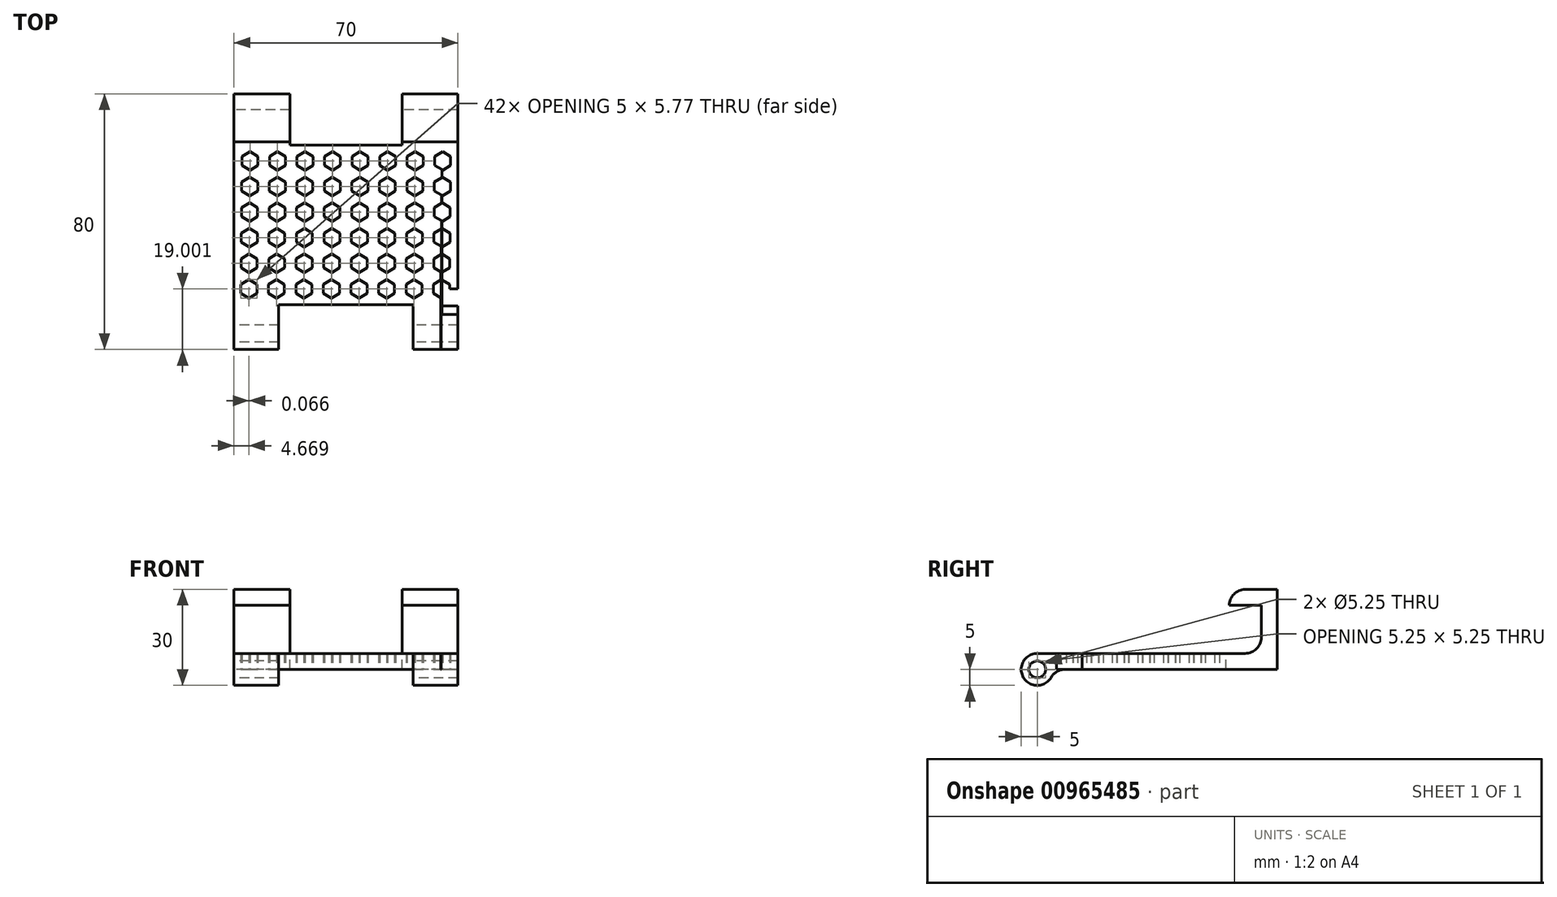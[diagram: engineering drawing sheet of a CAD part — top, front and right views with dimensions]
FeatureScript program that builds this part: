
annotation { "Feature Type Name" : "Feature", "Feature Type Description" : "" }
export const myFeature = defineFeature(function(context is Context, id is Id, definition is map)
    precondition{}
    {
        {
            var Q0;
            Q0=qCreatedBy(makeId("Right.planeOp"),FACE);
            var sketch = newSketch(context, id + "F0", { "sketchPlane" : qUnion([Q0])});
            skLineSegment(sketch, "E0", {"start": v(-20.34, 0) * mm, "end": v(0, 0) * mm, "construction": true});
            skLineSegment(sketch, "E1.0", {"start": v(-75, 14.81) * mm, "end": v(-75, 5) * mm, "construction": true});
            skLineSegment(sketch, "E2.0", {"start": v(-15, 25) * mm, "end": v(0, 25) * mm, "construction": true});
            skLineSegment(sketch, "E3.0", {"start": v(-20.34, 5) * mm, "end": v(-5, 5) * mm});
            skLineSegment(sketch, "E4", {"start": v(-20.34, 5) * mm, "end": v(-75, 5) * mm});
            skLineSegment(sketch, "E5", {"start": v(-66.34, 0) * mm, "end": v(0, 0) * mm});
            skLineSegment(sketch, "E6", {"start": v(0, 25) * mm, "end": v(-15, 25) * mm});
            skLineSegment(sketch, "E7", {"start": v(-15, 25) * mm, "end": v(-15, 20) * mm});
            skLineSegment(sketch, "E8", {"start": v(-15, 20) * mm, "end": v(-5, 20) * mm});
            skLineSegment(sketch, "E9", {"start": v(-5, 20) * mm, "end": v(-5, 5) * mm});
            skPoint(sketch, "E10.orphan", {"position": v(0, 14.81) * mm});
            skPoint(sketch, "E11.orphan", {"position": v(20.06, 25) * mm});
            skPoint(sketch, "E12.orphan", {"position": v(-20.06, 25) * mm});
            skLineSegment(sketch, "E13", {"start": v(0, 25) * mm, "end": v(0, 5) * mm});
            skLineSegment(sketch, "E14", {"start": v(0, 5) * mm, "end": v(0, 0) * mm});
            skArc(sketch, "E15", {"start": v(-75, 5) * mm, "mid": v(-79.33, -2.5) * mm, "end": v(-70.67, -2.5) * mm});
            skLineSegment(sketch, "E16.trimOffspring", {"start": v(-75, 0) * mm, "end": v(-75, -12.94) * mm, "construction": true});
            skCircle(sketch, "E17", {"center": v(-75, 0) * mm, "radius": 2.62 * mm});
            skPoint(sketch, "E18.visualSharp", {"position": v(-70, 0) * mm});
            skArc(sketch, "E18.filletArc", {"start": v(-66.34, 0) * mm, "mid": v(-68.84, -0.67) * mm, "end": v(-70.67, -2.5) * mm});
            skSolve(sketch);
        }
        {
            var Q0;
            Q0=makeQuery(id+"F0.imprint","IMPRINT",FACE,{"disambiguationData":[TD([[makeQuery(id+"F0.imprint","IMPRINT",EDGE,{"derivedFrom":sQuery(id+"F0.wireOp",EDGE,"E3.0")}),-1.0]])]});
            extrude(context, id + "F1", {"entities" : qUnion([Q0]), "depth" : 70 * mm, "offsetDistance" : 25 * mm});
        }
        {
            var Q0;
            Q0=qCreatedBy(makeId("Front.planeOp"),FACE);
            var sketch = newSketch(context, id + "F2", { "sketchPlane" : qUnion([Q0])});
            skLineSegment(sketch, "E19", {"start": v(0, 0) * mm, "end": v(0, 33.65) * mm, "construction": true});
            skLineSegment(sketch, "E20", {"start": v(0, 0) * mm, "end": v(85.21, 0) * mm, "construction": true});
            skLineSegment(sketch, "E21.0", {"start": v(17.5, 0) * mm, "end": v(17.5, 33.65) * mm, "construction": true});
            skLineSegment(sketch, "E22.0", {"start": v(0, 5) * mm, "end": v(85.21, 5) * mm, "construction": true});
            skLineSegment(sketch, "E23.bottom", {"start": v(17.5, 0) * mm, "end": v(52.5, 0) * mm});
            skLineSegment(sketch, "E23.top", {"start": v(17.5, 25) * mm, "end": v(52.5, 25) * mm});
            skLineSegment(sketch, "E23.left", {"start": v(17.5, 0) * mm, "end": v(17.5, 25) * mm});
            skLineSegment(sketch, "E23.right", {"start": v(52.5, 0) * mm, "end": v(52.5, 25) * mm});
            skSolve(sketch);
        }
        {
            var Q0;
            Q0 = qSketchRegion(id + "F2", true);
            extrude(context, id + "F3", {"entities" : qUnion([Q0]), "operationType" : NewBodyOperationType.REMOVE, "depth" : 16 * mm, "offsetDistance" : 25 * mm});
        }
        {
            var Q0;
            Q0=qCreatedBy(makeId("Front.planeOp"),FACE);
            cPlane(context, id + "F4", {"entities" : qUnion([Q0]), "cplaneType" : CPlaneType.OFFSET, "offset" : 75 * mm, "width" : 150 * mm, "height" : 150 * mm});
        }
        {
            var Q0;
            Q0=qCreatedBy(id+"F4.planeOp",FACE);
            var sketch = newSketch(context, id + "F5", { "sketchPlane" : qUnion([Q0])});
            skLineSegment(sketch, "E24", {"start": v(0, 31.01) * mm, "end": v(0, -27.06) * mm, "construction": true});
            skLineSegment(sketch, "E25.0", {"start": v(14, 31.01) * mm, "end": v(14, -27.06) * mm, "construction": true});
            skLineSegment(sketch, "E26.0", {"start": v(28, 31.01) * mm, "end": v(28, -27.06) * mm, "construction": true});
            skLineSegment(sketch, "E27.0", {"start": v(42, 31.01) * mm, "end": v(42, -27.06) * mm, "construction": true});
            skLineSegment(sketch, "E28.0", {"start": v(56, 31.01) * mm, "end": v(56, -27.06) * mm, "construction": true});
            skLineSegment(sketch, "E29.0", {"start": v(70, 31.01) * mm, "end": v(70, -27.06) * mm, "construction": true});
            skLineSegment(sketch, "E30.bottom", {"start": v(14, 5) * mm, "end": v(56, 5) * mm});
            skLineSegment(sketch, "E30.top", {"start": v(14, -5) * mm, "end": v(56, -5) * mm});
            skLineSegment(sketch, "E30.left", {"start": v(14, 5) * mm, "end": v(14, -5) * mm});
            skLineSegment(sketch, "E30.right", {"start": v(56, 5) * mm, "end": v(56, -5) * mm});
            skSolve(sketch);
        }
        {
            var Q0;
            Q0 = qSketchRegion(id + "F5", true);
            extrude(context, id + "F6", {"entities" : qUnion([Q0]), "operationType" : NewBodyOperationType.REMOVE, "oppositeDirection" : true, "depth" : 9 * mm, "offsetDistance" : 25 * mm, "hasSecondDirection" : true, "secondDirectionBound" : SecondDirectionBoundingType.THROUGH_ALL, "secondDirectionOppositeDirection" : false, "secondDirectionDepth" : 8 * mm});
        }
        {
            var Q0;
            {var subQ1=sQuery(id+"F0.wireOp",EDGE,"E3.0");var subQ2=sQuery(id+"F0.wireOp",EDGE,"E9");Q0=makeQuery(id+"F3.boolean.opBoolean","SPLIT",EDGE,{"disambiguationData":[TD([makeQuery(id+"F3.opExtrude","SWEPT_FACE",FACE,{"disambiguationData":[OSD([sQuery(id+"F2.wireOp",EDGE,"E23.left")])]})])],"derivedFrom":makeQuery(id+"F1.opExtrude","SWEPT_EDGE",EDGE,{"disambiguationData":[OSD([subQ1,subQ2])]})});}
            var Q1;
            {var subQ1=sQuery(id+"F0.wireOp",EDGE,"E3.0");var subQ2=sQuery(id+"F0.wireOp",EDGE,"E9");Q1=makeQuery(id+"F3.boolean.opBoolean","SPLIT",EDGE,{"disambiguationData":[TD([makeQuery(id+"F3.opExtrude","SWEPT_FACE",FACE,{"disambiguationData":[OSD([sQuery(id+"F2.wireOp",EDGE,"E23.right")])]})])],"derivedFrom":makeQuery(id+"F1.opExtrude","SWEPT_EDGE",EDGE,{"disambiguationData":[OSD([subQ1,subQ2])]})});}
            fillet(context, id + "F7", {"entities" : qUnion([Q0, Q1]), "radius" : 5 * mm, "tangentPropagation" : true, "allowEdgeOverflow" : false});
        }
        {
            var Q0;
            {var subQ0=sQuery(id+"F0.wireOp",EDGE,"E7");var subQ1=sQuery(id+"F0.wireOp",EDGE,"E6");Q0=makeQuery(id+"F3.boolean.opBoolean","SPLIT",EDGE,{"disambiguationData":[TD([makeQuery(id+"F3.opExtrude","SWEPT_FACE",FACE,{"disambiguationData":[OSD([sQuery(id+"F2.wireOp",EDGE,"E23.left")])]})])],"derivedFrom":makeQuery(id+"F1.opExtrude","SWEPT_EDGE",EDGE,{"disambiguationData":[OSD([subQ1,subQ0])]})});}
            var Q1;
            {var subQ0=sQuery(id+"F0.wireOp",EDGE,"E7");var subQ1=sQuery(id+"F0.wireOp",EDGE,"E6");Q1=makeQuery(id+"F3.boolean.opBoolean","SPLIT",EDGE,{"disambiguationData":[TD([makeQuery(id+"F3.opExtrude","SWEPT_FACE",FACE,{"disambiguationData":[OSD([sQuery(id+"F2.wireOp",EDGE,"E23.right")])]})])],"derivedFrom":makeQuery(id+"F1.opExtrude","SWEPT_EDGE",EDGE,{"disambiguationData":[OSD([subQ1,subQ0])]})});}
            fillet(context, id + "F8", {"entities" : qUnion([Q0, Q1]), "radius" : 5 * mm, "tangentPropagation" : true, "allowEdgeOverflow" : false});
        }
        {
            var Q0;
            Q0=qCreatedBy(makeId("Top.planeOp"),FACE);
            var sketch = newSketch(context, id + "F9", { "sketchPlane" : qUnion([Q0])});
            skLineSegment(sketch, "E31", {"start": v(17.5, -16) * mm, "end": v(-16.9, -16) * mm, "construction": true});
            skLineSegment(sketch, "E32", {"start": v(0, -9.91) * mm, "end": v(0, -88.84) * mm, "construction": true});
            skLineSegment(sketch, "E33.0", {"start": v(5, -4.91) * mm, "end": v(5, -83.84) * mm, "construction": true});
            skLineSegment(sketch, "E34.0", {"start": v(17.5, -21) * mm, "end": v(-16.9, -21) * mm, "construction": true});
            skLineSegment(sketch, "E35.0", {"start": v(2.5, -19.56) * mm, "end": v(5, -18.11) * mm});
            skLineSegment(sketch, "E35.1", {"start": v(5, -18.11) * mm, "end": v(7.5, -19.56) * mm});
            skLineSegment(sketch, "E35.2", {"start": v(7.5, -19.56) * mm, "end": v(7.5, -22.44) * mm});
            skLineSegment(sketch, "E35.3", {"start": v(7.5, -22.44) * mm, "end": v(5, -23.89) * mm});
            skLineSegment(sketch, "E35.4", {"start": v(5, -23.89) * mm, "end": v(2.5, -22.44) * mm});
            skLineSegment(sketch, "E35.5", {"start": v(2.5, -22.44) * mm, "end": v(2.5, -19.56) * mm});
            skPoint(sketch, "E35.0.midPoint", {"position": v(3.75, -18.83) * mm});
            skLineSegment(sketch, "E36", {"start": v(70, -84.15) * mm, "end": v(70, -10.08) * mm, "construction": true});
            skLineSegment(sketch, "E37", {"start": v(-10.15, -66) * mm, "end": v(71.85, -66) * mm, "construction": true});
            skLineSegment(sketch, "E38.0", {"start": v(-10.15, -61) * mm, "end": v(71.85, -61) * mm});
            skLineSegment(sketch, "E39.0", {"start": v(65, -84.15) * mm, "end": v(65, -10.08) * mm});
            skLineSegment(sketch, "E40.0.1.0", {"start": v(-10.22, -69) * mm, "end": v(71.78, -69) * mm});
            skLineSegment(sketch, "E40.0.1.1", {"start": v(64.93, -92.15) * mm, "end": v(64.93, -18.08) * mm});
            skLineSegment(sketch, "E40.0.1.2", {"start": v(2.43, -30.44) * mm, "end": v(2.43, -27.56) * mm});
            skLineSegment(sketch, "E40.0.1.3", {"start": v(4.93, -31.89) * mm, "end": v(2.43, -30.44) * mm});
            skLineSegment(sketch, "E40.0.1.4", {"start": v(7.43, -30.44) * mm, "end": v(4.93, -31.89) * mm});
            skLineSegment(sketch, "E40.0.1.5", {"start": v(7.43, -27.56) * mm, "end": v(7.43, -30.44) * mm});
            skLineSegment(sketch, "E40.0.1.6", {"start": v(4.93, -26.11) * mm, "end": v(7.43, -27.56) * mm});
            skLineSegment(sketch, "E40.0.1.7", {"start": v(2.43, -27.56) * mm, "end": v(4.93, -26.11) * mm});
            skLineSegment(sketch, "E40.0.2.0", {"start": v(-10.28, -77) * mm, "end": v(71.72, -77) * mm});
            skLineSegment(sketch, "E40.0.2.1", {"start": v(64.87, -100.15) * mm, "end": v(64.87, -26.08) * mm});
            skLineSegment(sketch, "E40.0.2.2", {"start": v(2.37, -38.44) * mm, "end": v(2.37, -35.56) * mm});
            skLineSegment(sketch, "E40.0.2.3", {"start": v(4.87, -39.89) * mm, "end": v(2.37, -38.44) * mm});
            skLineSegment(sketch, "E40.0.2.4", {"start": v(7.37, -38.44) * mm, "end": v(4.87, -39.89) * mm});
            skLineSegment(sketch, "E40.0.2.5", {"start": v(7.37, -35.56) * mm, "end": v(7.37, -38.44) * mm});
            skLineSegment(sketch, "E40.0.2.6", {"start": v(4.87, -34.11) * mm, "end": v(7.37, -35.56) * mm});
            skLineSegment(sketch, "E40.0.2.7", {"start": v(2.37, -35.56) * mm, "end": v(4.87, -34.11) * mm});
            skLineSegment(sketch, "E40.0.3.0", {"start": v(-10.35, -85) * mm, "end": v(71.65, -85) * mm});
            skLineSegment(sketch, "E40.0.3.1", {"start": v(64.8, -108.15) * mm, "end": v(64.8, -34.08) * mm});
            skLineSegment(sketch, "E40.0.3.2", {"start": v(2.3, -46.44) * mm, "end": v(2.3, -43.56) * mm});
            skLineSegment(sketch, "E40.0.3.3", {"start": v(4.8, -47.89) * mm, "end": v(2.3, -46.44) * mm});
            skLineSegment(sketch, "E40.0.3.4", {"start": v(7.3, -46.44) * mm, "end": v(4.8, -47.89) * mm});
            skLineSegment(sketch, "E40.0.3.5", {"start": v(7.3, -43.56) * mm, "end": v(7.3, -46.44) * mm});
            skLineSegment(sketch, "E40.0.3.6", {"start": v(4.8, -42.11) * mm, "end": v(7.3, -43.56) * mm});
            skLineSegment(sketch, "E40.0.3.7", {"start": v(2.3, -43.56) * mm, "end": v(4.8, -42.11) * mm});
            skLineSegment(sketch, "E40.0.4.0", {"start": v(-10.42, -93) * mm, "end": v(71.58, -93) * mm});
            skLineSegment(sketch, "E40.0.4.1", {"start": v(64.74, -116.15) * mm, "end": v(64.74, -42.08) * mm});
            skLineSegment(sketch, "E40.0.4.2", {"start": v(2.24, -54.44) * mm, "end": v(2.24, -51.56) * mm});
            skLineSegment(sketch, "E40.0.4.3", {"start": v(4.74, -55.89) * mm, "end": v(2.24, -54.44) * mm});
            skLineSegment(sketch, "E40.0.4.4", {"start": v(7.24, -54.44) * mm, "end": v(4.74, -55.89) * mm});
            skLineSegment(sketch, "E40.0.4.5", {"start": v(7.24, -51.56) * mm, "end": v(7.24, -54.44) * mm});
            skLineSegment(sketch, "E40.0.4.6", {"start": v(4.74, -50.11) * mm, "end": v(7.24, -51.56) * mm});
            skLineSegment(sketch, "E40.0.4.7", {"start": v(2.24, -51.56) * mm, "end": v(4.74, -50.11) * mm});
            skLineSegment(sketch, "E40.0.5.0", {"start": v(-10.48, -101) * mm, "end": v(71.52, -101) * mm});
            skLineSegment(sketch, "E40.0.5.1", {"start": v(64.67, -124.15) * mm, "end": v(64.67, -50.08) * mm});
            skLineSegment(sketch, "E40.0.5.2", {"start": v(2.17, -62.44) * mm, "end": v(2.17, -59.56) * mm});
            skLineSegment(sketch, "E40.0.5.3", {"start": v(4.67, -63.89) * mm, "end": v(2.17, -62.44) * mm});
            skLineSegment(sketch, "E40.0.5.4", {"start": v(7.17, -62.44) * mm, "end": v(4.67, -63.89) * mm});
            skLineSegment(sketch, "E40.0.5.5", {"start": v(7.17, -59.56) * mm, "end": v(7.17, -62.44) * mm});
            skLineSegment(sketch, "E40.0.5.6", {"start": v(4.67, -58.11) * mm, "end": v(7.17, -59.56) * mm});
            skLineSegment(sketch, "E40.0.5.7", {"start": v(2.17, -59.56) * mm, "end": v(4.67, -58.11) * mm});
            skLineSegment(sketch, "E40.1.0.0", {"start": v(-1.55, -61) * mm, "end": v(80.45, -61) * mm});
            skLineSegment(sketch, "E40.1.0.1", {"start": v(73.6, -84.15) * mm, "end": v(73.6, -10.08) * mm});
            skLineSegment(sketch, "E40.1.0.2", {"start": v(11.1, -22.44) * mm, "end": v(11.1, -19.56) * mm});
            skLineSegment(sketch, "E40.1.0.3", {"start": v(13.6, -23.89) * mm, "end": v(11.1, -22.44) * mm});
            skLineSegment(sketch, "E40.1.0.4", {"start": v(16.1, -22.44) * mm, "end": v(13.6, -23.89) * mm});
            skLineSegment(sketch, "E40.1.0.5", {"start": v(16.1, -19.56) * mm, "end": v(16.1, -22.44) * mm});
            skLineSegment(sketch, "E40.1.0.6", {"start": v(13.6, -18.11) * mm, "end": v(16.1, -19.56) * mm});
            skLineSegment(sketch, "E40.1.0.7", {"start": v(11.1, -19.56) * mm, "end": v(13.6, -18.11) * mm});
            skLineSegment(sketch, "E40.1.1.0", {"start": v(-1.62, -69) * mm, "end": v(80.38, -69) * mm});
            skLineSegment(sketch, "E40.1.1.1", {"start": v(73.53, -92.15) * mm, "end": v(73.53, -18.08) * mm});
            skLineSegment(sketch, "E40.1.1.2", {"start": v(11.03, -30.44) * mm, "end": v(11.03, -27.56) * mm});
            skLineSegment(sketch, "E40.1.1.3", {"start": v(13.53, -31.89) * mm, "end": v(11.03, -30.44) * mm});
            skLineSegment(sketch, "E40.1.1.4", {"start": v(16.03, -30.44) * mm, "end": v(13.53, -31.89) * mm});
            skLineSegment(sketch, "E40.1.1.5", {"start": v(16.03, -27.56) * mm, "end": v(16.03, -30.44) * mm});
            skLineSegment(sketch, "E40.1.1.6", {"start": v(13.53, -26.11) * mm, "end": v(16.03, -27.56) * mm});
            skLineSegment(sketch, "E40.1.1.7", {"start": v(11.03, -27.56) * mm, "end": v(13.53, -26.11) * mm});
            skLineSegment(sketch, "E40.1.2.0", {"start": v(-1.68, -77) * mm, "end": v(80.32, -77) * mm});
            skLineSegment(sketch, "E40.1.2.1", {"start": v(73.47, -100.15) * mm, "end": v(73.47, -26.08) * mm});
            skLineSegment(sketch, "E40.1.2.2", {"start": v(10.97, -38.44) * mm, "end": v(10.97, -35.56) * mm});
            skLineSegment(sketch, "E40.1.2.3", {"start": v(13.47, -39.89) * mm, "end": v(10.97, -38.44) * mm});
            skLineSegment(sketch, "E40.1.2.4", {"start": v(15.97, -38.44) * mm, "end": v(13.47, -39.89) * mm});
            skLineSegment(sketch, "E40.1.2.5", {"start": v(15.97, -35.56) * mm, "end": v(15.97, -38.44) * mm});
            skLineSegment(sketch, "E40.1.2.6", {"start": v(13.47, -34.11) * mm, "end": v(15.97, -35.56) * mm});
            skLineSegment(sketch, "E40.1.2.7", {"start": v(10.97, -35.56) * mm, "end": v(13.47, -34.11) * mm});
            skLineSegment(sketch, "E40.1.3.0", {"start": v(-1.75, -85) * mm, "end": v(80.25, -85) * mm});
            skLineSegment(sketch, "E40.1.3.1", {"start": v(73.4, -108.15) * mm, "end": v(73.4, -34.08) * mm});
            skLineSegment(sketch, "E40.1.3.2", {"start": v(10.9, -46.44) * mm, "end": v(10.9, -43.56) * mm});
            skLineSegment(sketch, "E40.1.3.3", {"start": v(13.4, -47.89) * mm, "end": v(10.9, -46.44) * mm});
            skLineSegment(sketch, "E40.1.3.4", {"start": v(15.9, -46.44) * mm, "end": v(13.4, -47.89) * mm});
            skLineSegment(sketch, "E40.1.3.5", {"start": v(15.9, -43.56) * mm, "end": v(15.9, -46.44) * mm});
            skLineSegment(sketch, "E40.1.3.6", {"start": v(13.4, -42.11) * mm, "end": v(15.9, -43.56) * mm});
            skLineSegment(sketch, "E40.1.3.7", {"start": v(10.9, -43.56) * mm, "end": v(13.4, -42.11) * mm});
            skLineSegment(sketch, "E40.1.4.0", {"start": v(-1.82, -93) * mm, "end": v(80.18, -93) * mm});
            skLineSegment(sketch, "E40.1.4.1", {"start": v(73.34, -116.15) * mm, "end": v(73.34, -42.08) * mm});
            skLineSegment(sketch, "E40.1.4.2", {"start": v(10.84, -54.44) * mm, "end": v(10.84, -51.56) * mm});
            skLineSegment(sketch, "E40.1.4.3", {"start": v(13.34, -55.89) * mm, "end": v(10.84, -54.44) * mm});
            skLineSegment(sketch, "E40.1.4.4", {"start": v(15.84, -54.44) * mm, "end": v(13.34, -55.89) * mm});
            skLineSegment(sketch, "E40.1.4.5", {"start": v(15.84, -51.56) * mm, "end": v(15.84, -54.44) * mm});
            skLineSegment(sketch, "E40.1.4.6", {"start": v(13.34, -50.11) * mm, "end": v(15.84, -51.56) * mm});
            skLineSegment(sketch, "E40.1.4.7", {"start": v(10.84, -51.56) * mm, "end": v(13.34, -50.11) * mm});
            skLineSegment(sketch, "E40.1.5.0", {"start": v(-1.88, -101) * mm, "end": v(80.12, -101) * mm});
            skLineSegment(sketch, "E40.1.5.1", {"start": v(73.27, -124.15) * mm, "end": v(73.27, -50.08) * mm});
            skLineSegment(sketch, "E40.1.5.2", {"start": v(10.77, -62.44) * mm, "end": v(10.77, -59.56) * mm});
            skLineSegment(sketch, "E40.1.5.3", {"start": v(13.27, -63.89) * mm, "end": v(10.77, -62.44) * mm});
            skLineSegment(sketch, "E40.1.5.4", {"start": v(15.77, -62.44) * mm, "end": v(13.27, -63.89) * mm});
            skLineSegment(sketch, "E40.1.5.5", {"start": v(15.77, -59.56) * mm, "end": v(15.77, -62.44) * mm});
            skLineSegment(sketch, "E40.1.5.6", {"start": v(13.27, -58.11) * mm, "end": v(15.77, -59.56) * mm});
            skLineSegment(sketch, "E40.1.5.7", {"start": v(10.77, -59.56) * mm, "end": v(13.27, -58.11) * mm});
            skLineSegment(sketch, "E40.2.0.0", {"start": v(7.05, -61) * mm, "end": v(89.05, -61) * mm});
            skLineSegment(sketch, "E40.2.0.1", {"start": v(82.2, -84.15) * mm, "end": v(82.2, -10.08) * mm});
            skLineSegment(sketch, "E40.2.0.2", {"start": v(19.7, -22.44) * mm, "end": v(19.7, -19.56) * mm});
            skLineSegment(sketch, "E40.2.0.3", {"start": v(22.2, -23.89) * mm, "end": v(19.7, -22.44) * mm});
            skLineSegment(sketch, "E40.2.0.4", {"start": v(24.7, -22.44) * mm, "end": v(22.2, -23.89) * mm});
            skLineSegment(sketch, "E40.2.0.5", {"start": v(24.7, -19.56) * mm, "end": v(24.7, -22.44) * mm});
            skLineSegment(sketch, "E40.2.0.6", {"start": v(22.2, -18.11) * mm, "end": v(24.7, -19.56) * mm});
            skLineSegment(sketch, "E40.2.0.7", {"start": v(19.7, -19.56) * mm, "end": v(22.2, -18.11) * mm});
            skLineSegment(sketch, "E40.2.1.0", {"start": v(6.98, -69) * mm, "end": v(88.98, -69) * mm});
            skLineSegment(sketch, "E40.2.1.1", {"start": v(82.13, -92.15) * mm, "end": v(82.13, -18.08) * mm});
            skLineSegment(sketch, "E40.2.1.2", {"start": v(19.63, -30.44) * mm, "end": v(19.63, -27.56) * mm});
            skLineSegment(sketch, "E40.2.1.3", {"start": v(22.13, -31.89) * mm, "end": v(19.63, -30.44) * mm});
            skLineSegment(sketch, "E40.2.1.4", {"start": v(24.63, -30.44) * mm, "end": v(22.13, -31.89) * mm});
            skLineSegment(sketch, "E40.2.1.5", {"start": v(24.63, -27.56) * mm, "end": v(24.63, -30.44) * mm});
            skLineSegment(sketch, "E40.2.1.6", {"start": v(22.13, -26.11) * mm, "end": v(24.63, -27.56) * mm});
            skLineSegment(sketch, "E40.2.1.7", {"start": v(19.63, -27.56) * mm, "end": v(22.13, -26.11) * mm});
            skLineSegment(sketch, "E40.2.2.0", {"start": v(6.92, -77) * mm, "end": v(88.92, -77) * mm});
            skLineSegment(sketch, "E40.2.2.1", {"start": v(82.07, -100.15) * mm, "end": v(82.07, -26.08) * mm});
            skLineSegment(sketch, "E40.2.2.2", {"start": v(19.57, -38.44) * mm, "end": v(19.57, -35.56) * mm});
            skLineSegment(sketch, "E40.2.2.3", {"start": v(22.07, -39.89) * mm, "end": v(19.57, -38.44) * mm});
            skLineSegment(sketch, "E40.2.2.4", {"start": v(24.57, -38.44) * mm, "end": v(22.07, -39.89) * mm});
            skLineSegment(sketch, "E40.2.2.5", {"start": v(24.57, -35.56) * mm, "end": v(24.57, -38.44) * mm});
            skLineSegment(sketch, "E40.2.2.6", {"start": v(22.07, -34.11) * mm, "end": v(24.57, -35.56) * mm});
            skLineSegment(sketch, "E40.2.2.7", {"start": v(19.57, -35.56) * mm, "end": v(22.07, -34.11) * mm});
            skLineSegment(sketch, "E40.2.3.0", {"start": v(6.85, -85) * mm, "end": v(88.85, -85) * mm});
            skLineSegment(sketch, "E40.2.3.1", {"start": v(82, -108.15) * mm, "end": v(82, -34.08) * mm});
            skLineSegment(sketch, "E40.2.3.2", {"start": v(19.5, -46.44) * mm, "end": v(19.5, -43.56) * mm});
            skLineSegment(sketch, "E40.2.3.3", {"start": v(22, -47.89) * mm, "end": v(19.5, -46.44) * mm});
            skLineSegment(sketch, "E40.2.3.4", {"start": v(24.5, -46.44) * mm, "end": v(22, -47.89) * mm});
            skLineSegment(sketch, "E40.2.3.5", {"start": v(24.5, -43.56) * mm, "end": v(24.5, -46.44) * mm});
            skLineSegment(sketch, "E40.2.3.6", {"start": v(22, -42.11) * mm, "end": v(24.5, -43.56) * mm});
            skLineSegment(sketch, "E40.2.3.7", {"start": v(19.5, -43.56) * mm, "end": v(22, -42.11) * mm});
            skLineSegment(sketch, "E40.2.4.0", {"start": v(6.78, -93) * mm, "end": v(88.78, -93) * mm});
            skLineSegment(sketch, "E40.2.4.1", {"start": v(81.94, -116.15) * mm, "end": v(81.94, -42.08) * mm});
            skLineSegment(sketch, "E40.2.4.2", {"start": v(19.44, -54.44) * mm, "end": v(19.44, -51.56) * mm});
            skLineSegment(sketch, "E40.2.4.3", {"start": v(21.94, -55.89) * mm, "end": v(19.44, -54.44) * mm});
            skLineSegment(sketch, "E40.2.4.4", {"start": v(24.44, -54.44) * mm, "end": v(21.94, -55.89) * mm});
            skLineSegment(sketch, "E40.2.4.5", {"start": v(24.44, -51.56) * mm, "end": v(24.44, -54.44) * mm});
            skLineSegment(sketch, "E40.2.4.6", {"start": v(21.94, -50.11) * mm, "end": v(24.44, -51.56) * mm});
            skLineSegment(sketch, "E40.2.4.7", {"start": v(19.44, -51.56) * mm, "end": v(21.94, -50.11) * mm});
            skLineSegment(sketch, "E40.2.5.0", {"start": v(6.72, -101) * mm, "end": v(88.72, -101) * mm});
            skLineSegment(sketch, "E40.2.5.1", {"start": v(81.87, -124.15) * mm, "end": v(81.87, -50.08) * mm});
            skLineSegment(sketch, "E40.2.5.2", {"start": v(19.37, -62.44) * mm, "end": v(19.37, -59.56) * mm});
            skLineSegment(sketch, "E40.2.5.3", {"start": v(21.87, -63.89) * mm, "end": v(19.37, -62.44) * mm});
            skLineSegment(sketch, "E40.2.5.4", {"start": v(24.37, -62.44) * mm, "end": v(21.87, -63.89) * mm});
            skLineSegment(sketch, "E40.2.5.5", {"start": v(24.37, -59.56) * mm, "end": v(24.37, -62.44) * mm});
            skLineSegment(sketch, "E40.2.5.6", {"start": v(21.87, -58.11) * mm, "end": v(24.37, -59.56) * mm});
            skLineSegment(sketch, "E40.2.5.7", {"start": v(19.37, -59.56) * mm, "end": v(21.87, -58.11) * mm});
            skLineSegment(sketch, "E40.3.0.0", {"start": v(15.65, -61) * mm, "end": v(97.65, -61) * mm});
            skLineSegment(sketch, "E40.3.0.1", {"start": v(90.8, -84.15) * mm, "end": v(90.8, -10.08) * mm});
            skLineSegment(sketch, "E40.3.0.2", {"start": v(28.3, -22.44) * mm, "end": v(28.3, -19.56) * mm});
            skLineSegment(sketch, "E40.3.0.3", {"start": v(30.8, -23.89) * mm, "end": v(28.3, -22.44) * mm});
            skLineSegment(sketch, "E40.3.0.4", {"start": v(33.3, -22.44) * mm, "end": v(30.8, -23.89) * mm});
            skLineSegment(sketch, "E40.3.0.5", {"start": v(33.3, -19.56) * mm, "end": v(33.3, -22.44) * mm});
            skLineSegment(sketch, "E40.3.0.6", {"start": v(30.8, -18.11) * mm, "end": v(33.3, -19.56) * mm});
            skLineSegment(sketch, "E40.3.0.7", {"start": v(28.3, -19.56) * mm, "end": v(30.8, -18.11) * mm});
            skLineSegment(sketch, "E40.3.1.0", {"start": v(15.58, -69) * mm, "end": v(97.58, -69) * mm});
            skLineSegment(sketch, "E40.3.1.1", {"start": v(90.73, -92.15) * mm, "end": v(90.73, -18.08) * mm});
            skLineSegment(sketch, "E40.3.1.2", {"start": v(28.23, -30.44) * mm, "end": v(28.23, -27.56) * mm});
            skLineSegment(sketch, "E40.3.1.3", {"start": v(30.73, -31.89) * mm, "end": v(28.23, -30.44) * mm});
            skLineSegment(sketch, "E40.3.1.4", {"start": v(33.23, -30.44) * mm, "end": v(30.73, -31.89) * mm});
            skLineSegment(sketch, "E40.3.1.5", {"start": v(33.23, -27.56) * mm, "end": v(33.23, -30.44) * mm});
            skLineSegment(sketch, "E40.3.1.6", {"start": v(30.73, -26.11) * mm, "end": v(33.23, -27.56) * mm});
            skLineSegment(sketch, "E40.3.1.7", {"start": v(28.23, -27.56) * mm, "end": v(30.73, -26.11) * mm});
            skLineSegment(sketch, "E40.3.2.0", {"start": v(15.52, -77) * mm, "end": v(97.52, -77) * mm});
            skLineSegment(sketch, "E40.3.2.1", {"start": v(90.67, -100.15) * mm, "end": v(90.67, -26.08) * mm});
            skLineSegment(sketch, "E40.3.2.2", {"start": v(28.17, -38.44) * mm, "end": v(28.17, -35.56) * mm});
            skLineSegment(sketch, "E40.3.2.3", {"start": v(30.67, -39.89) * mm, "end": v(28.17, -38.44) * mm});
            skLineSegment(sketch, "E40.3.2.4", {"start": v(33.17, -38.44) * mm, "end": v(30.67, -39.89) * mm});
            skLineSegment(sketch, "E40.3.2.5", {"start": v(33.17, -35.56) * mm, "end": v(33.17, -38.44) * mm});
            skLineSegment(sketch, "E40.3.2.6", {"start": v(30.67, -34.11) * mm, "end": v(33.17, -35.56) * mm});
            skLineSegment(sketch, "E40.3.2.7", {"start": v(28.17, -35.56) * mm, "end": v(30.67, -34.11) * mm});
            skLineSegment(sketch, "E40.3.3.0", {"start": v(15.45, -85) * mm, "end": v(97.45, -85) * mm});
            skLineSegment(sketch, "E40.3.3.1", {"start": v(90.6, -108.15) * mm, "end": v(90.6, -34.08) * mm});
            skLineSegment(sketch, "E40.3.3.2", {"start": v(28.1, -46.44) * mm, "end": v(28.1, -43.56) * mm});
            skLineSegment(sketch, "E40.3.3.3", {"start": v(30.6, -47.89) * mm, "end": v(28.1, -46.44) * mm});
            skLineSegment(sketch, "E40.3.3.4", {"start": v(33.1, -46.44) * mm, "end": v(30.6, -47.89) * mm});
            skLineSegment(sketch, "E40.3.3.5", {"start": v(33.1, -43.56) * mm, "end": v(33.1, -46.44) * mm});
            skLineSegment(sketch, "E40.3.3.6", {"start": v(30.6, -42.11) * mm, "end": v(33.1, -43.56) * mm});
            skLineSegment(sketch, "E40.3.3.7", {"start": v(28.1, -43.56) * mm, "end": v(30.6, -42.11) * mm});
            skLineSegment(sketch, "E40.3.4.0", {"start": v(15.38, -93) * mm, "end": v(97.38, -93) * mm});
            skLineSegment(sketch, "E40.3.4.1", {"start": v(90.54, -116.15) * mm, "end": v(90.54, -42.08) * mm});
            skLineSegment(sketch, "E40.3.4.2", {"start": v(28.04, -54.44) * mm, "end": v(28.04, -51.56) * mm});
            skLineSegment(sketch, "E40.3.4.3", {"start": v(30.54, -55.89) * mm, "end": v(28.04, -54.44) * mm});
            skLineSegment(sketch, "E40.3.4.4", {"start": v(33.04, -54.44) * mm, "end": v(30.54, -55.89) * mm});
            skLineSegment(sketch, "E40.3.4.5", {"start": v(33.04, -51.56) * mm, "end": v(33.04, -54.44) * mm});
            skLineSegment(sketch, "E40.3.4.6", {"start": v(30.54, -50.11) * mm, "end": v(33.04, -51.56) * mm});
            skLineSegment(sketch, "E40.3.4.7", {"start": v(28.04, -51.56) * mm, "end": v(30.54, -50.11) * mm});
            skLineSegment(sketch, "E40.3.5.0", {"start": v(15.32, -101) * mm, "end": v(97.32, -101) * mm});
            skLineSegment(sketch, "E40.3.5.1", {"start": v(90.47, -124.15) * mm, "end": v(90.47, -50.08) * mm});
            skLineSegment(sketch, "E40.3.5.2", {"start": v(27.97, -62.44) * mm, "end": v(27.97, -59.56) * mm});
            skLineSegment(sketch, "E40.3.5.3", {"start": v(30.47, -63.89) * mm, "end": v(27.97, -62.44) * mm});
            skLineSegment(sketch, "E40.3.5.4", {"start": v(32.97, -62.44) * mm, "end": v(30.47, -63.89) * mm});
            skLineSegment(sketch, "E40.3.5.5", {"start": v(32.97, -59.56) * mm, "end": v(32.97, -62.44) * mm});
            skLineSegment(sketch, "E40.3.5.6", {"start": v(30.47, -58.11) * mm, "end": v(32.97, -59.56) * mm});
            skLineSegment(sketch, "E40.3.5.7", {"start": v(27.97, -59.56) * mm, "end": v(30.47, -58.11) * mm});
            skLineSegment(sketch, "E40.4.0.0", {"start": v(24.25, -61) * mm, "end": v(106.25, -61) * mm});
            skLineSegment(sketch, "E40.4.0.1", {"start": v(99.4, -84.15) * mm, "end": v(99.4, -10.08) * mm});
            skLineSegment(sketch, "E40.4.0.2", {"start": v(36.9, -22.44) * mm, "end": v(36.9, -19.56) * mm});
            skLineSegment(sketch, "E40.4.0.3", {"start": v(39.4, -23.89) * mm, "end": v(36.9, -22.44) * mm});
            skLineSegment(sketch, "E40.4.0.4", {"start": v(41.9, -22.44) * mm, "end": v(39.4, -23.89) * mm});
            skLineSegment(sketch, "E40.4.0.5", {"start": v(41.9, -19.56) * mm, "end": v(41.9, -22.44) * mm});
            skLineSegment(sketch, "E40.4.0.6", {"start": v(39.4, -18.11) * mm, "end": v(41.9, -19.56) * mm});
            skLineSegment(sketch, "E40.4.0.7", {"start": v(36.9, -19.56) * mm, "end": v(39.4, -18.11) * mm});
            skLineSegment(sketch, "E40.4.1.0", {"start": v(24.18, -69) * mm, "end": v(106.18, -69) * mm});
            skLineSegment(sketch, "E40.4.1.1", {"start": v(99.33, -92.15) * mm, "end": v(99.33, -18.08) * mm});
            skLineSegment(sketch, "E40.4.1.2", {"start": v(36.83, -30.44) * mm, "end": v(36.83, -27.56) * mm});
            skLineSegment(sketch, "E40.4.1.3", {"start": v(39.33, -31.89) * mm, "end": v(36.83, -30.44) * mm});
            skLineSegment(sketch, "E40.4.1.4", {"start": v(41.83, -30.44) * mm, "end": v(39.33, -31.89) * mm});
            skLineSegment(sketch, "E40.4.1.5", {"start": v(41.83, -27.56) * mm, "end": v(41.83, -30.44) * mm});
            skLineSegment(sketch, "E40.4.1.6", {"start": v(39.33, -26.11) * mm, "end": v(41.83, -27.56) * mm});
            skLineSegment(sketch, "E40.4.1.7", {"start": v(36.83, -27.56) * mm, "end": v(39.33, -26.11) * mm});
            skLineSegment(sketch, "E40.4.2.0", {"start": v(24.12, -77) * mm, "end": v(106.12, -77) * mm});
            skLineSegment(sketch, "E40.4.2.1", {"start": v(99.27, -100.15) * mm, "end": v(99.27, -26.08) * mm});
            skLineSegment(sketch, "E40.4.2.2", {"start": v(36.77, -38.44) * mm, "end": v(36.77, -35.56) * mm});
            skLineSegment(sketch, "E40.4.2.3", {"start": v(39.27, -39.89) * mm, "end": v(36.77, -38.44) * mm});
            skLineSegment(sketch, "E40.4.2.4", {"start": v(41.77, -38.44) * mm, "end": v(39.27, -39.89) * mm});
            skLineSegment(sketch, "E40.4.2.5", {"start": v(41.77, -35.56) * mm, "end": v(41.77, -38.44) * mm});
            skLineSegment(sketch, "E40.4.2.6", {"start": v(39.27, -34.11) * mm, "end": v(41.77, -35.56) * mm});
            skLineSegment(sketch, "E40.4.2.7", {"start": v(36.77, -35.56) * mm, "end": v(39.27, -34.11) * mm});
            skLineSegment(sketch, "E40.4.3.0", {"start": v(24.05, -85) * mm, "end": v(106.05, -85) * mm});
            skLineSegment(sketch, "E40.4.3.1", {"start": v(99.2, -108.15) * mm, "end": v(99.2, -34.08) * mm});
            skLineSegment(sketch, "E40.4.3.2", {"start": v(36.7, -46.44) * mm, "end": v(36.7, -43.56) * mm});
            skLineSegment(sketch, "E40.4.3.3", {"start": v(39.2, -47.89) * mm, "end": v(36.7, -46.44) * mm});
            skLineSegment(sketch, "E40.4.3.4", {"start": v(41.7, -46.44) * mm, "end": v(39.2, -47.89) * mm});
            skLineSegment(sketch, "E40.4.3.5", {"start": v(41.7, -43.56) * mm, "end": v(41.7, -46.44) * mm});
            skLineSegment(sketch, "E40.4.3.6", {"start": v(39.2, -42.11) * mm, "end": v(41.7, -43.56) * mm});
            skLineSegment(sketch, "E40.4.3.7", {"start": v(36.7, -43.56) * mm, "end": v(39.2, -42.11) * mm});
            skLineSegment(sketch, "E40.4.4.0", {"start": v(23.98, -93) * mm, "end": v(105.98, -93) * mm});
            skLineSegment(sketch, "E40.4.4.1", {"start": v(99.14, -116.15) * mm, "end": v(99.14, -42.08) * mm});
            skLineSegment(sketch, "E40.4.4.2", {"start": v(36.64, -54.44) * mm, "end": v(36.64, -51.56) * mm});
            skLineSegment(sketch, "E40.4.4.3", {"start": v(39.14, -55.89) * mm, "end": v(36.64, -54.44) * mm});
            skLineSegment(sketch, "E40.4.4.4", {"start": v(41.64, -54.44) * mm, "end": v(39.14, -55.89) * mm});
            skLineSegment(sketch, "E40.4.4.5", {"start": v(41.64, -51.56) * mm, "end": v(41.64, -54.44) * mm});
            skLineSegment(sketch, "E40.4.4.6", {"start": v(39.14, -50.11) * mm, "end": v(41.64, -51.56) * mm});
            skLineSegment(sketch, "E40.4.4.7", {"start": v(36.64, -51.56) * mm, "end": v(39.14, -50.11) * mm});
            skLineSegment(sketch, "E40.4.5.0", {"start": v(23.92, -101) * mm, "end": v(105.92, -101) * mm});
            skLineSegment(sketch, "E40.4.5.1", {"start": v(99.07, -124.15) * mm, "end": v(99.07, -50.08) * mm});
            skLineSegment(sketch, "E40.4.5.2", {"start": v(36.57, -62.44) * mm, "end": v(36.57, -59.56) * mm});
            skLineSegment(sketch, "E40.4.5.3", {"start": v(39.07, -63.89) * mm, "end": v(36.57, -62.44) * mm});
            skLineSegment(sketch, "E40.4.5.4", {"start": v(41.57, -62.44) * mm, "end": v(39.07, -63.89) * mm});
            skLineSegment(sketch, "E40.4.5.5", {"start": v(41.57, -59.56) * mm, "end": v(41.57, -62.44) * mm});
            skLineSegment(sketch, "E40.4.5.6", {"start": v(39.07, -58.11) * mm, "end": v(41.57, -59.56) * mm});
            skLineSegment(sketch, "E40.4.5.7", {"start": v(36.57, -59.56) * mm, "end": v(39.07, -58.11) * mm});
            skLineSegment(sketch, "E40.5.0.0", {"start": v(32.85, -61) * mm, "end": v(114.85, -61) * mm});
            skLineSegment(sketch, "E40.5.0.1", {"start": v(108, -84.15) * mm, "end": v(108, -10.08) * mm});
            skLineSegment(sketch, "E40.5.0.2", {"start": v(45.5, -22.44) * mm, "end": v(45.5, -19.56) * mm});
            skLineSegment(sketch, "E40.5.0.3", {"start": v(48, -23.89) * mm, "end": v(45.5, -22.44) * mm});
            skLineSegment(sketch, "E40.5.0.4", {"start": v(50.5, -22.44) * mm, "end": v(48, -23.89) * mm});
            skLineSegment(sketch, "E40.5.0.5", {"start": v(50.5, -19.56) * mm, "end": v(50.5, -22.44) * mm});
            skLineSegment(sketch, "E40.5.0.6", {"start": v(48, -18.11) * mm, "end": v(50.5, -19.56) * mm});
            skLineSegment(sketch, "E40.5.0.7", {"start": v(45.5, -19.56) * mm, "end": v(48, -18.11) * mm});
            skLineSegment(sketch, "E40.5.1.0", {"start": v(32.78, -69) * mm, "end": v(114.78, -69) * mm});
            skLineSegment(sketch, "E40.5.1.1", {"start": v(107.93, -92.15) * mm, "end": v(107.93, -18.08) * mm});
            skLineSegment(sketch, "E40.5.1.2", {"start": v(45.43, -30.44) * mm, "end": v(45.43, -27.56) * mm});
            skLineSegment(sketch, "E40.5.1.3", {"start": v(47.93, -31.89) * mm, "end": v(45.43, -30.44) * mm});
            skLineSegment(sketch, "E40.5.1.4", {"start": v(50.43, -30.44) * mm, "end": v(47.93, -31.89) * mm});
            skLineSegment(sketch, "E40.5.1.5", {"start": v(50.43, -27.56) * mm, "end": v(50.43, -30.44) * mm});
            skLineSegment(sketch, "E40.5.1.6", {"start": v(47.93, -26.11) * mm, "end": v(50.43, -27.56) * mm});
            skLineSegment(sketch, "E40.5.1.7", {"start": v(45.43, -27.56) * mm, "end": v(47.93, -26.11) * mm});
            skLineSegment(sketch, "E40.5.2.0", {"start": v(32.72, -77) * mm, "end": v(114.72, -77) * mm});
            skLineSegment(sketch, "E40.5.2.1", {"start": v(107.87, -100.15) * mm, "end": v(107.87, -26.08) * mm});
            skLineSegment(sketch, "E40.5.2.2", {"start": v(45.37, -38.44) * mm, "end": v(45.37, -35.56) * mm});
            skLineSegment(sketch, "E40.5.2.3", {"start": v(47.87, -39.89) * mm, "end": v(45.37, -38.44) * mm});
            skLineSegment(sketch, "E40.5.2.4", {"start": v(50.37, -38.44) * mm, "end": v(47.87, -39.89) * mm});
            skLineSegment(sketch, "E40.5.2.5", {"start": v(50.37, -35.56) * mm, "end": v(50.37, -38.44) * mm});
            skLineSegment(sketch, "E40.5.2.6", {"start": v(47.87, -34.11) * mm, "end": v(50.37, -35.56) * mm});
            skLineSegment(sketch, "E40.5.2.7", {"start": v(45.37, -35.56) * mm, "end": v(47.87, -34.11) * mm});
            skLineSegment(sketch, "E40.5.3.0", {"start": v(32.65, -85) * mm, "end": v(114.65, -85) * mm});
            skLineSegment(sketch, "E40.5.3.1", {"start": v(107.8, -108.15) * mm, "end": v(107.8, -34.08) * mm});
            skLineSegment(sketch, "E40.5.3.2", {"start": v(45.3, -46.44) * mm, "end": v(45.3, -43.56) * mm});
            skLineSegment(sketch, "E40.5.3.3", {"start": v(47.8, -47.89) * mm, "end": v(45.3, -46.44) * mm});
            skLineSegment(sketch, "E40.5.3.4", {"start": v(50.3, -46.44) * mm, "end": v(47.8, -47.89) * mm});
            skLineSegment(sketch, "E40.5.3.5", {"start": v(50.3, -43.56) * mm, "end": v(50.3, -46.44) * mm});
            skLineSegment(sketch, "E40.5.3.6", {"start": v(47.8, -42.11) * mm, "end": v(50.3, -43.56) * mm});
            skLineSegment(sketch, "E40.5.3.7", {"start": v(45.3, -43.56) * mm, "end": v(47.8, -42.11) * mm});
            skLineSegment(sketch, "E40.5.4.0", {"start": v(32.58, -93) * mm, "end": v(114.58, -93) * mm});
            skLineSegment(sketch, "E40.5.4.1", {"start": v(107.74, -116.15) * mm, "end": v(107.74, -42.08) * mm});
            skLineSegment(sketch, "E40.5.4.2", {"start": v(45.24, -54.44) * mm, "end": v(45.24, -51.56) * mm});
            skLineSegment(sketch, "E40.5.4.3", {"start": v(47.74, -55.89) * mm, "end": v(45.24, -54.44) * mm});
            skLineSegment(sketch, "E40.5.4.4", {"start": v(50.24, -54.44) * mm, "end": v(47.74, -55.89) * mm});
            skLineSegment(sketch, "E40.5.4.5", {"start": v(50.24, -51.56) * mm, "end": v(50.24, -54.44) * mm});
            skLineSegment(sketch, "E40.5.4.6", {"start": v(47.74, -50.11) * mm, "end": v(50.24, -51.56) * mm});
            skLineSegment(sketch, "E40.5.4.7", {"start": v(45.24, -51.56) * mm, "end": v(47.74, -50.11) * mm});
            skLineSegment(sketch, "E40.5.5.0", {"start": v(32.52, -101) * mm, "end": v(114.52, -101) * mm});
            skLineSegment(sketch, "E40.5.5.1", {"start": v(107.67, -124.15) * mm, "end": v(107.67, -50.08) * mm});
            skLineSegment(sketch, "E40.5.5.2", {"start": v(45.17, -62.44) * mm, "end": v(45.17, -59.56) * mm});
            skLineSegment(sketch, "E40.5.5.3", {"start": v(47.67, -63.89) * mm, "end": v(45.17, -62.44) * mm});
            skLineSegment(sketch, "E40.5.5.4", {"start": v(50.17, -62.44) * mm, "end": v(47.67, -63.89) * mm});
            skLineSegment(sketch, "E40.5.5.5", {"start": v(50.17, -59.56) * mm, "end": v(50.17, -62.44) * mm});
            skLineSegment(sketch, "E40.5.5.6", {"start": v(47.67, -58.11) * mm, "end": v(50.17, -59.56) * mm});
            skLineSegment(sketch, "E40.5.5.7", {"start": v(45.17, -59.56) * mm, "end": v(47.67, -58.11) * mm});
            skLineSegment(sketch, "E40.6.0.0", {"start": v(41.45, -61) * mm, "end": v(123.45, -61) * mm});
            skLineSegment(sketch, "E40.6.0.1", {"start": v(116.6, -84.15) * mm, "end": v(116.6, -10.08) * mm});
            skLineSegment(sketch, "E40.6.0.2", {"start": v(54.1, -22.44) * mm, "end": v(54.1, -19.56) * mm});
            skLineSegment(sketch, "E40.6.0.3", {"start": v(56.6, -23.89) * mm, "end": v(54.1, -22.44) * mm});
            skLineSegment(sketch, "E40.6.0.4", {"start": v(59.1, -22.44) * mm, "end": v(56.6, -23.89) * mm});
            skLineSegment(sketch, "E40.6.0.5", {"start": v(59.1, -19.56) * mm, "end": v(59.1, -22.44) * mm});
            skLineSegment(sketch, "E40.6.0.6", {"start": v(56.6, -18.11) * mm, "end": v(59.1, -19.56) * mm});
            skLineSegment(sketch, "E40.6.0.7", {"start": v(54.1, -19.56) * mm, "end": v(56.6, -18.11) * mm});
            skLineSegment(sketch, "E40.6.1.0", {"start": v(41.38, -69) * mm, "end": v(123.38, -69) * mm});
            skLineSegment(sketch, "E40.6.1.1", {"start": v(116.53, -92.15) * mm, "end": v(116.53, -18.08) * mm});
            skLineSegment(sketch, "E40.6.1.2", {"start": v(54.03, -30.44) * mm, "end": v(54.03, -27.56) * mm});
            skLineSegment(sketch, "E40.6.1.3", {"start": v(56.53, -31.89) * mm, "end": v(54.03, -30.44) * mm});
            skLineSegment(sketch, "E40.6.1.4", {"start": v(59.03, -30.44) * mm, "end": v(56.53, -31.89) * mm});
            skLineSegment(sketch, "E40.6.1.5", {"start": v(59.03, -27.56) * mm, "end": v(59.03, -30.44) * mm});
            skLineSegment(sketch, "E40.6.1.6", {"start": v(56.53, -26.11) * mm, "end": v(59.03, -27.56) * mm});
            skLineSegment(sketch, "E40.6.1.7", {"start": v(54.03, -27.56) * mm, "end": v(56.53, -26.11) * mm});
            skLineSegment(sketch, "E40.6.2.0", {"start": v(41.32, -77) * mm, "end": v(123.32, -77) * mm});
            skLineSegment(sketch, "E40.6.2.1", {"start": v(116.47, -100.15) * mm, "end": v(116.47, -26.08) * mm});
            skLineSegment(sketch, "E40.6.2.2", {"start": v(53.97, -38.44) * mm, "end": v(53.97, -35.56) * mm});
            skLineSegment(sketch, "E40.6.2.3", {"start": v(56.47, -39.89) * mm, "end": v(53.97, -38.44) * mm});
            skLineSegment(sketch, "E40.6.2.4", {"start": v(58.97, -38.44) * mm, "end": v(56.47, -39.89) * mm});
            skLineSegment(sketch, "E40.6.2.5", {"start": v(58.97, -35.56) * mm, "end": v(58.97, -38.44) * mm});
            skLineSegment(sketch, "E40.6.2.6", {"start": v(56.47, -34.11) * mm, "end": v(58.97, -35.56) * mm});
            skLineSegment(sketch, "E40.6.2.7", {"start": v(53.97, -35.56) * mm, "end": v(56.47, -34.11) * mm});
            skLineSegment(sketch, "E40.6.3.0", {"start": v(41.25, -85) * mm, "end": v(123.25, -85) * mm});
            skLineSegment(sketch, "E40.6.3.1", {"start": v(116.4, -108.15) * mm, "end": v(116.4, -34.08) * mm});
            skLineSegment(sketch, "E40.6.3.2", {"start": v(53.9, -46.44) * mm, "end": v(53.9, -43.56) * mm});
            skLineSegment(sketch, "E40.6.3.3", {"start": v(56.4, -47.89) * mm, "end": v(53.9, -46.44) * mm});
            skLineSegment(sketch, "E40.6.3.4", {"start": v(58.9, -46.44) * mm, "end": v(56.4, -47.89) * mm});
            skLineSegment(sketch, "E40.6.3.5", {"start": v(58.9, -43.56) * mm, "end": v(58.9, -46.44) * mm});
            skLineSegment(sketch, "E40.6.3.6", {"start": v(56.4, -42.11) * mm, "end": v(58.9, -43.56) * mm});
            skLineSegment(sketch, "E40.6.3.7", {"start": v(53.9, -43.56) * mm, "end": v(56.4, -42.11) * mm});
            skLineSegment(sketch, "E40.6.4.0", {"start": v(41.18, -93) * mm, "end": v(123.18, -93) * mm});
            skLineSegment(sketch, "E40.6.4.1", {"start": v(116.34, -116.15) * mm, "end": v(116.34, -42.08) * mm});
            skLineSegment(sketch, "E40.6.4.2", {"start": v(53.84, -54.44) * mm, "end": v(53.84, -51.56) * mm});
            skLineSegment(sketch, "E40.6.4.3", {"start": v(56.34, -55.89) * mm, "end": v(53.84, -54.44) * mm});
            skLineSegment(sketch, "E40.6.4.4", {"start": v(58.84, -54.44) * mm, "end": v(56.34, -55.89) * mm});
            skLineSegment(sketch, "E40.6.4.5", {"start": v(58.84, -51.56) * mm, "end": v(58.84, -54.44) * mm});
            skLineSegment(sketch, "E40.6.4.6", {"start": v(56.34, -50.11) * mm, "end": v(58.84, -51.56) * mm});
            skLineSegment(sketch, "E40.6.4.7", {"start": v(53.84, -51.56) * mm, "end": v(56.34, -50.11) * mm});
            skLineSegment(sketch, "E40.6.5.0", {"start": v(41.12, -101) * mm, "end": v(123.12, -101) * mm});
            skLineSegment(sketch, "E40.6.5.1", {"start": v(116.27, -124.15) * mm, "end": v(116.27, -50.08) * mm});
            skLineSegment(sketch, "E40.6.5.2", {"start": v(53.77, -62.44) * mm, "end": v(53.77, -59.56) * mm});
            skLineSegment(sketch, "E40.6.5.3", {"start": v(56.27, -63.89) * mm, "end": v(53.77, -62.44) * mm});
            skLineSegment(sketch, "E40.6.5.4", {"start": v(58.77, -62.44) * mm, "end": v(56.27, -63.89) * mm});
            skLineSegment(sketch, "E40.6.5.5", {"start": v(58.77, -59.56) * mm, "end": v(58.77, -62.44) * mm});
            skLineSegment(sketch, "E40.6.5.6", {"start": v(56.27, -58.11) * mm, "end": v(58.77, -59.56) * mm});
            skLineSegment(sketch, "E40.6.5.7", {"start": v(53.77, -59.56) * mm, "end": v(56.27, -58.11) * mm});
            skLineSegment(sketch, "E40.7.0.0", {"start": v(50.05, -61) * mm, "end": v(132.05, -61) * mm});
            skLineSegment(sketch, "E40.7.0.1", {"start": v(125.2, -84.15) * mm, "end": v(125.2, -10.08) * mm});
            skLineSegment(sketch, "E40.7.0.2", {"start": v(62.7, -22.44) * mm, "end": v(62.7, -19.56) * mm});
            skLineSegment(sketch, "E40.7.0.3", {"start": v(65.2, -23.89) * mm, "end": v(62.7, -22.44) * mm});
            skLineSegment(sketch, "E40.7.0.4", {"start": v(67.7, -22.44) * mm, "end": v(65.2, -23.89) * mm});
            skLineSegment(sketch, "E40.7.0.5", {"start": v(67.7, -19.56) * mm, "end": v(67.7, -22.44) * mm});
            skLineSegment(sketch, "E40.7.0.6", {"start": v(65.2, -18.11) * mm, "end": v(67.7, -19.56) * mm});
            skLineSegment(sketch, "E40.7.0.7", {"start": v(62.7, -19.56) * mm, "end": v(65.2, -18.11) * mm});
            skLineSegment(sketch, "E40.7.1.0", {"start": v(49.98, -69) * mm, "end": v(131.98, -69) * mm});
            skLineSegment(sketch, "E40.7.1.1", {"start": v(125.13, -92.15) * mm, "end": v(125.13, -18.08) * mm});
            skLineSegment(sketch, "E40.7.1.2", {"start": v(62.63, -30.44) * mm, "end": v(62.63, -27.56) * mm});
            skLineSegment(sketch, "E40.7.1.3", {"start": v(65.13, -31.89) * mm, "end": v(62.63, -30.44) * mm});
            skLineSegment(sketch, "E40.7.1.4", {"start": v(67.63, -30.44) * mm, "end": v(65.13, -31.89) * mm});
            skLineSegment(sketch, "E40.7.1.5", {"start": v(67.63, -27.56) * mm, "end": v(67.63, -30.44) * mm});
            skLineSegment(sketch, "E40.7.1.6", {"start": v(65.13, -26.11) * mm, "end": v(67.63, -27.56) * mm});
            skLineSegment(sketch, "E40.7.1.7", {"start": v(62.63, -27.56) * mm, "end": v(65.13, -26.11) * mm});
            skLineSegment(sketch, "E40.7.2.0", {"start": v(49.92, -77) * mm, "end": v(131.92, -77) * mm});
            skLineSegment(sketch, "E40.7.2.1", {"start": v(125.07, -100.15) * mm, "end": v(125.07, -26.08) * mm});
            skLineSegment(sketch, "E40.7.2.2", {"start": v(62.57, -38.44) * mm, "end": v(62.57, -35.56) * mm});
            skLineSegment(sketch, "E40.7.2.3", {"start": v(65.07, -39.89) * mm, "end": v(62.57, -38.44) * mm});
            skLineSegment(sketch, "E40.7.2.4", {"start": v(67.57, -38.44) * mm, "end": v(65.07, -39.89) * mm});
            skLineSegment(sketch, "E40.7.2.5", {"start": v(67.57, -35.56) * mm, "end": v(67.57, -38.44) * mm});
            skLineSegment(sketch, "E40.7.2.6", {"start": v(65.07, -34.11) * mm, "end": v(67.57, -35.56) * mm});
            skLineSegment(sketch, "E40.7.2.7", {"start": v(62.57, -35.56) * mm, "end": v(65.07, -34.11) * mm});
            skLineSegment(sketch, "E40.7.3.0", {"start": v(49.85, -85) * mm, "end": v(131.85, -85) * mm});
            skLineSegment(sketch, "E40.7.3.1", {"start": v(125, -108.15) * mm, "end": v(125, -34.08) * mm});
            skLineSegment(sketch, "E40.7.3.2", {"start": v(62.5, -46.44) * mm, "end": v(62.5, -43.56) * mm});
            skLineSegment(sketch, "E40.7.3.3", {"start": v(65, -47.89) * mm, "end": v(62.5, -46.44) * mm});
            skLineSegment(sketch, "E40.7.3.4", {"start": v(67.5, -46.44) * mm, "end": v(65, -47.89) * mm});
            skLineSegment(sketch, "E40.7.3.5", {"start": v(67.5, -43.56) * mm, "end": v(67.5, -46.44) * mm});
            skLineSegment(sketch, "E40.7.3.6", {"start": v(65, -42.11) * mm, "end": v(67.5, -43.56) * mm});
            skLineSegment(sketch, "E40.7.3.7", {"start": v(62.5, -43.56) * mm, "end": v(65, -42.11) * mm});
            skLineSegment(sketch, "E40.7.4.0", {"start": v(49.78, -93) * mm, "end": v(131.78, -93) * mm});
            skLineSegment(sketch, "E40.7.4.1", {"start": v(124.94, -116.15) * mm, "end": v(124.94, -42.08) * mm});
            skLineSegment(sketch, "E40.7.4.2", {"start": v(62.44, -54.44) * mm, "end": v(62.44, -51.56) * mm});
            skLineSegment(sketch, "E40.7.4.3", {"start": v(64.94, -55.89) * mm, "end": v(62.44, -54.44) * mm});
            skLineSegment(sketch, "E40.7.4.4", {"start": v(67.44, -54.44) * mm, "end": v(64.94, -55.89) * mm});
            skLineSegment(sketch, "E40.7.4.5", {"start": v(67.44, -51.56) * mm, "end": v(67.44, -54.44) * mm});
            skLineSegment(sketch, "E40.7.4.6", {"start": v(64.94, -50.11) * mm, "end": v(67.44, -51.56) * mm});
            skLineSegment(sketch, "E40.7.4.7", {"start": v(62.44, -51.56) * mm, "end": v(64.94, -50.11) * mm});
            skLineSegment(sketch, "E40.7.5.0", {"start": v(49.72, -101) * mm, "end": v(131.72, -101) * mm});
            skLineSegment(sketch, "E40.7.5.1", {"start": v(124.87, -124.15) * mm, "end": v(124.87, -50.08) * mm});
            skLineSegment(sketch, "E40.7.5.2", {"start": v(62.37, -62.44) * mm, "end": v(62.37, -59.56) * mm});
            skLineSegment(sketch, "E40.7.5.3", {"start": v(64.87, -63.89) * mm, "end": v(62.37, -62.44) * mm});
            skLineSegment(sketch, "E40.7.5.4", {"start": v(67.37, -62.44) * mm, "end": v(64.87, -63.89) * mm});
            skLineSegment(sketch, "E40.7.5.5", {"start": v(67.37, -59.56) * mm, "end": v(67.37, -62.44) * mm});
            skLineSegment(sketch, "E40.7.5.6", {"start": v(64.87, -58.11) * mm, "end": v(67.37, -59.56) * mm});
            skLineSegment(sketch, "E40.7.5.7", {"start": v(62.37, -59.56) * mm, "end": v(64.87, -58.11) * mm});
            skLineSegment(sketch, "E40.direction1", {"start": v(-10.15, -61) * mm, "end": v(-1.55, -61) * mm, "construction": true});
            skLineSegment(sketch, "E40.direction2", {"start": v(-10.15, -61) * mm, "end": v(-10.22, -69) * mm, "construction": true});
            skSolve(sketch);
        }
        {
            var Q0;
            Q0 = qSketchRegion(id + "F9", true);
            extrude(context, id + "F10", {"entities" : qUnion([Q0]), "operationType" : NewBodyOperationType.REMOVE, "depth" : 15 * mm, "offsetDistance" : 25 * mm});
        }
    });
